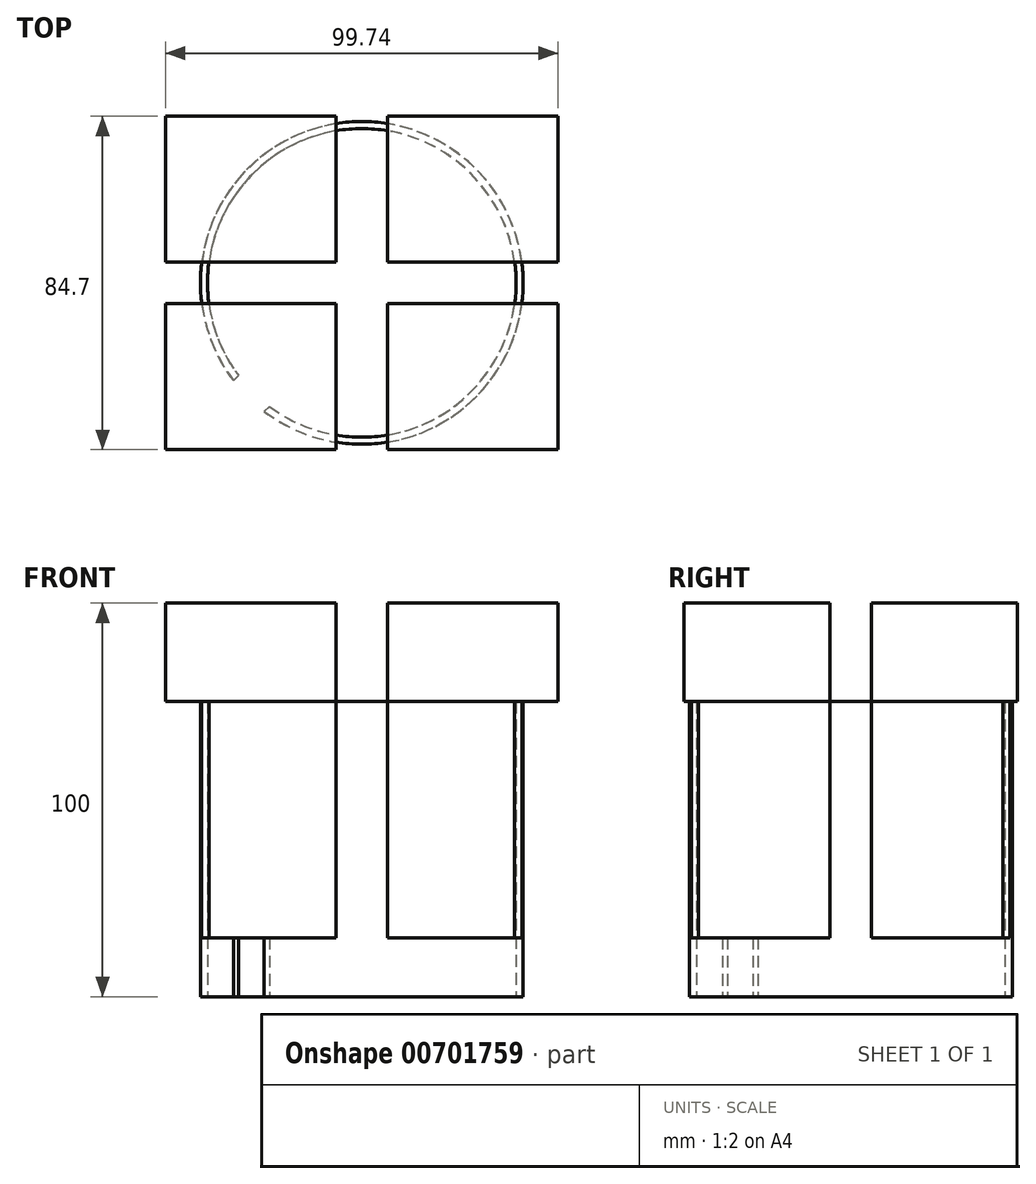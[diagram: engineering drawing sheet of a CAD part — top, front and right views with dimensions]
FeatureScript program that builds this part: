
annotation { "Feature Type Name" : "Feature", "Feature Type Description" : "" }
export const myFeature = defineFeature(function(context is Context, id is Id, definition is map)
    precondition{}
    {
        {
            var Q0;
            Q0=qCreatedBy(makeId("Top.planeOp"),FACE);
            var sketch = newSketch(context, id + "F0", { "sketchPlane" : qUnion([Q0])});
            skCircle(sketch, "E0", {"center": v(0, 0) * mm, "radius": 41 * mm});
            skSolve(sketch);
        }
        {
            var Q0;
            Q0 = qSketchRegion(id + "F0", true);
            extrude(context, id + "F1", {"entities" : qUnion([Q0]), "depth" : 75 * mm, "offsetDistance" : 25 * mm});
        }
        {
            var Q0;
            Q0=makeQuery(id+"F1.opExtrude","CAP_FACE",FACE,{"disambiguationData":[OSD([sQuery(id+"F0.wireOp",EDGE,"E0")])],"isStart":false});
            var Q1;
            Q1=makeQuery(id+"F1.opExtrude","CAP_FACE",FACE,{"disambiguationData":[OSD([sQuery(id+"F0.wireOp",EDGE,"E0")])],"isStart":true});
            shell(context, id + "F2", {"entities" : qUnion([Q0, Q1]), "thickness" : 1.8 * mm});
        }
        {
            var Q0;
            Q0=makeQuery(id+"F1.opExtrude","CAP_FACE",FACE,{"disambiguationData":[OSD([sQuery(id+"F0.wireOp",EDGE,"E0")])],"isStart":false});
            var sketch = newSketch(context, id + "F3", { "sketchPlane" : qUnion([Q0])});
            skLineSegment(sketch, "E1.bottom", {"start": v(-6.54, 5.27) * mm, "end": v(-49.87, 5.27) * mm});
            skLineSegment(sketch, "E1.top", {"start": v(-6.54, 42.35) * mm, "end": v(-49.87, 42.35) * mm});
            skLineSegment(sketch, "E1.left", {"start": v(-6.54, 5.27) * mm, "end": v(-6.54, 42.35) * mm});
            skLineSegment(sketch, "E1.right", {"start": v(-49.87, 5.27) * mm, "end": v(-49.87, 42.35) * mm});
            skSolve(sketch);
        }
        {
            var Q0;
            Q0 = qSketchRegion(id + "F3", true);
            extrude(context, id + "F4", {"entities" : qUnion([Q0]), "depth" : 25 * mm, "offsetDistance" : 25 * mm});
        }
        {
            var Q0;
            Q0=makeQuery(id+"F4.opExtrude","SWEPT_BODY",BODY,{"disambiguationData":[OSD([sQuery(id+"F3.wireOp",EDGE,"E1.bottom"),sQuery(id+"F3.wireOp",EDGE,"E1.top"),sQuery(id+"F3.wireOp",EDGE,"E1.left"),sQuery(id+"F3.wireOp",EDGE,"E1.right")])]});
            var Q1;
            Q1=qCreatedBy(makeId("Right.planeOp"),FACE);
            mirror(context, id + "F5", {"entities" : qUnion([Q0]), "mirrorPlane" : qUnion([Q1])});
        }
        {
            var Q0;
            Q0=makeQuery(id+"F4.opExtrude","SWEPT_BODY",BODY,{"disambiguationData":[OSD([sQuery(id+"F3.wireOp",EDGE,"E1.bottom"),sQuery(id+"F3.wireOp",EDGE,"E1.top"),sQuery(id+"F3.wireOp",EDGE,"E1.left"),sQuery(id+"F3.wireOp",EDGE,"E1.right")])]});
            var Q1;
            Q1=makeQuery(id+"F5.opPattern","COPY",BODY,{"derivedFrom":makeQuery(id+"F4.opExtrude","SWEPT_BODY",BODY,{"disambiguationData":[OSD([sQuery(id+"F3.wireOp",EDGE,"E1.bottom"),sQuery(id+"F3.wireOp",EDGE,"E1.top"),sQuery(id+"F3.wireOp",EDGE,"E1.left"),sQuery(id+"F3.wireOp",EDGE,"E1.right")])]}),"instanceName":"1"});
            var Q2;
            Q2=qCreatedBy(makeId("Front.planeOp"),FACE);
            mirror(context, id + "F6", {"entities" : qUnion([Q0, Q1]), "mirrorPlane" : qUnion([Q2])});
        }
        {
            var Q0;
            Q0=makeQuery(id+"F5.opPattern","COPY",FACE,{"derivedFrom":makeQuery(id+"F4.opExtrude","CAP_FACE",FACE,{"disambiguationData":[OSD([sQuery(id+"F3.wireOp",EDGE,"E1.bottom"),sQuery(id+"F3.wireOp",EDGE,"E1.top"),sQuery(id+"F3.wireOp",EDGE,"E1.left"),sQuery(id+"F3.wireOp",EDGE,"E1.right")])],"isStart":true}),"instanceName":"1"});
            var Q1;
            Q1=makeQuery(id+"F4.opExtrude","CAP_FACE",FACE,{"disambiguationData":[OSD([sQuery(id+"F3.wireOp",EDGE,"E1.bottom"),sQuery(id+"F3.wireOp",EDGE,"E1.top"),sQuery(id+"F3.wireOp",EDGE,"E1.left"),sQuery(id+"F3.wireOp",EDGE,"E1.right")])],"isStart":true});
            var Q2;
            Q2=makeQuery(id+"F6.opPattern","COPY",FACE,{"derivedFrom":makeQuery(id+"F4.opExtrude","CAP_FACE",FACE,{"disambiguationData":[OSD([sQuery(id+"F3.wireOp",EDGE,"E1.bottom"),sQuery(id+"F3.wireOp",EDGE,"E1.top"),sQuery(id+"F3.wireOp",EDGE,"E1.left"),sQuery(id+"F3.wireOp",EDGE,"E1.right")])],"isStart":true}),"instanceName":"1"});
            var Q3;
            Q3=makeQuery(id+"F6.opPattern","COPY",FACE,{"derivedFrom":makeQuery(id+"F5.opPattern","COPY",FACE,{"derivedFrom":makeQuery(id+"F4.opExtrude","CAP_FACE",FACE,{"disambiguationData":[OSD([sQuery(id+"F3.wireOp",EDGE,"E1.bottom"),sQuery(id+"F3.wireOp",EDGE,"E1.top"),sQuery(id+"F3.wireOp",EDGE,"E1.left"),sQuery(id+"F3.wireOp",EDGE,"E1.right")])],"isStart":true}),"instanceName":"1"}),"instanceName":"1"});
            extrude(context, id + "F7", {"entities" : qUnion([Q0, Q1, Q2, Q3]), "operationType" : NewBodyOperationType.REMOVE, "depth" : 60 * mm, "offsetDistance" : 25 * mm});
        }
        {
            var Q0;
            Q0=qCreatedBy(makeId("Top.planeOp"),FACE);
            var sketch = newSketch(context, id + "F8", { "sketchPlane" : qUnion([Q0])});
            skLineSegment(sketch, "E2.bottom", {"start": v(0, 0) * mm, "end": v(-30, 0) * mm, "construction": true});
            skLineSegment(sketch, "E2.top", {"start": v(0, -30) * mm, "end": v(-30, -30) * mm, "construction": true});
            skLineSegment(sketch, "E2.left", {"start": v(0, 0) * mm, "end": v(0, -30) * mm, "construction": true});
            skLineSegment(sketch, "E2.right", {"start": v(-30, 0) * mm, "end": v(-30, -30) * mm, "construction": true});
            skLineSegment(sketch, "E3", {"start": v(0, 0) * mm, "end": v(-30, -30) * mm, "construction": true});
            skSolve(sketch);
        }
        {
            var Q0;
            Q0=makeQuery(id+"F1.opExtrude","CAP_FACE",FACE,{"disambiguationData":[OSD([sQuery(id+"F0.wireOp",EDGE,"E0")])],"isStart":true});
            var sketch = newSketch(context, id + "F9", { "sketchPlane" : qUnion([Q0])});
            skLineSegment(sketch, "E4.bottom", {"start": v(-30, 30.04) * mm, "end": v(-22.16, 30.04) * mm});
            skLineSegment(sketch, "E4.top", {"start": v(-30, 22.2) * mm, "end": v(-22.16, 22.2) * mm});
            skLineSegment(sketch, "E4.left", {"start": v(-30, 30.04) * mm, "end": v(-30, 22.2) * mm});
            skLineSegment(sketch, "E4.right", {"start": v(-22.16, 30.04) * mm, "end": v(-22.16, 22.2) * mm});
            skLineSegment(sketch, "E5", {"start": v(-30, 22.2) * mm, "end": v(-33.9, 26.12) * mm});
            skLineSegment(sketch, "E6", {"start": v(-30, 30.04) * mm, "end": v(-33.9, 26.12) * mm});
            skLineSegment(sketch, "E7", {"start": v(-30, 30.04) * mm, "end": v(-26.08, 33.96) * mm});
            skLineSegment(sketch, "E8", {"start": v(-26.08, 33.96) * mm, "end": v(-22.16, 30.04) * mm});
            skSolve(sketch);
        }
        {
            var Q0;
            {var subQ1=sQuery(id+"F0.wireOp",EDGE,"E0");var subQ2=makeQuery(id+"F1.opExtrude","CAP_EDGE",EDGE,{"disambiguationData":[OSD([subQ1])],"isStart":true});var subQ6=sQuery(id+"F9.wireOp",EDGE,"E5");var subQ7=makeQuery(id+"F9.imprint","INTERSECT",VERTEX,{"derivedFrom":[subQ2,subQ6]});Q0=makeQuery(id+"F9.imprint","IMPRINT",FACE,{"disambiguationData":[TD([[makeQuery(id+"F9.imprint","IMPRINT",EDGE,{"disambiguationData":[TD([[subQ7,-1.0]])],"derivedFrom":subQ2}),-1.0]])]});}
            var Q1;
            {var subQ0=sQuery(id+"F9.wireOp",EDGE,"E4.bottom");var subQ1=sQuery(id+"F0.wireOp",EDGE,"E0");var subQ2=makeQuery(id+"F1.opExtrude","CAP_EDGE",EDGE,{"disambiguationData":[OSD([subQ1])],"isStart":true});var subQ3=makeQuery(id+"F9.imprint","INTERSECT",VERTEX,{"derivedFrom":[subQ2,subQ0]});Q1=makeQuery(id+"F9.imprint","IMPRINT",FACE,{"disambiguationData":[TD([[makeQuery(id+"F9.imprint","IMPRINT",EDGE,{"disambiguationData":[TD([[subQ3,1.0]])],"derivedFrom":subQ2}),-1.0]])]});}
            var Q2;
            {var subQ1=sQuery(id+"F0.wireOp",EDGE,"E0");var subQ2=makeQuery(id+"F1.opExtrude","CAP_EDGE",EDGE,{"disambiguationData":[OSD([subQ1])],"isStart":true});var subQ6=sQuery(id+"F9.wireOp",EDGE,"E8");var subQ8=makeQuery(id+"F9.imprint","INTERSECT",VERTEX,{"derivedFrom":[subQ2,subQ6]});Q2=makeQuery(id+"F9.imprint","IMPRINT",FACE,{"disambiguationData":[TD([[makeQuery(id+"F9.imprint","IMPRINT",EDGE,{"disambiguationData":[TD([[subQ8,1.0]])],"derivedFrom":subQ2}),-1.0]])]});}
            extrude(context, id + "F10", {"entities" : qUnion([Q0, Q1, Q2]), "operationType" : NewBodyOperationType.REMOVE, "oppositeDirection" : true, "depth" : 25 * mm, "offsetDistance" : 25 * mm});
        }
    });
